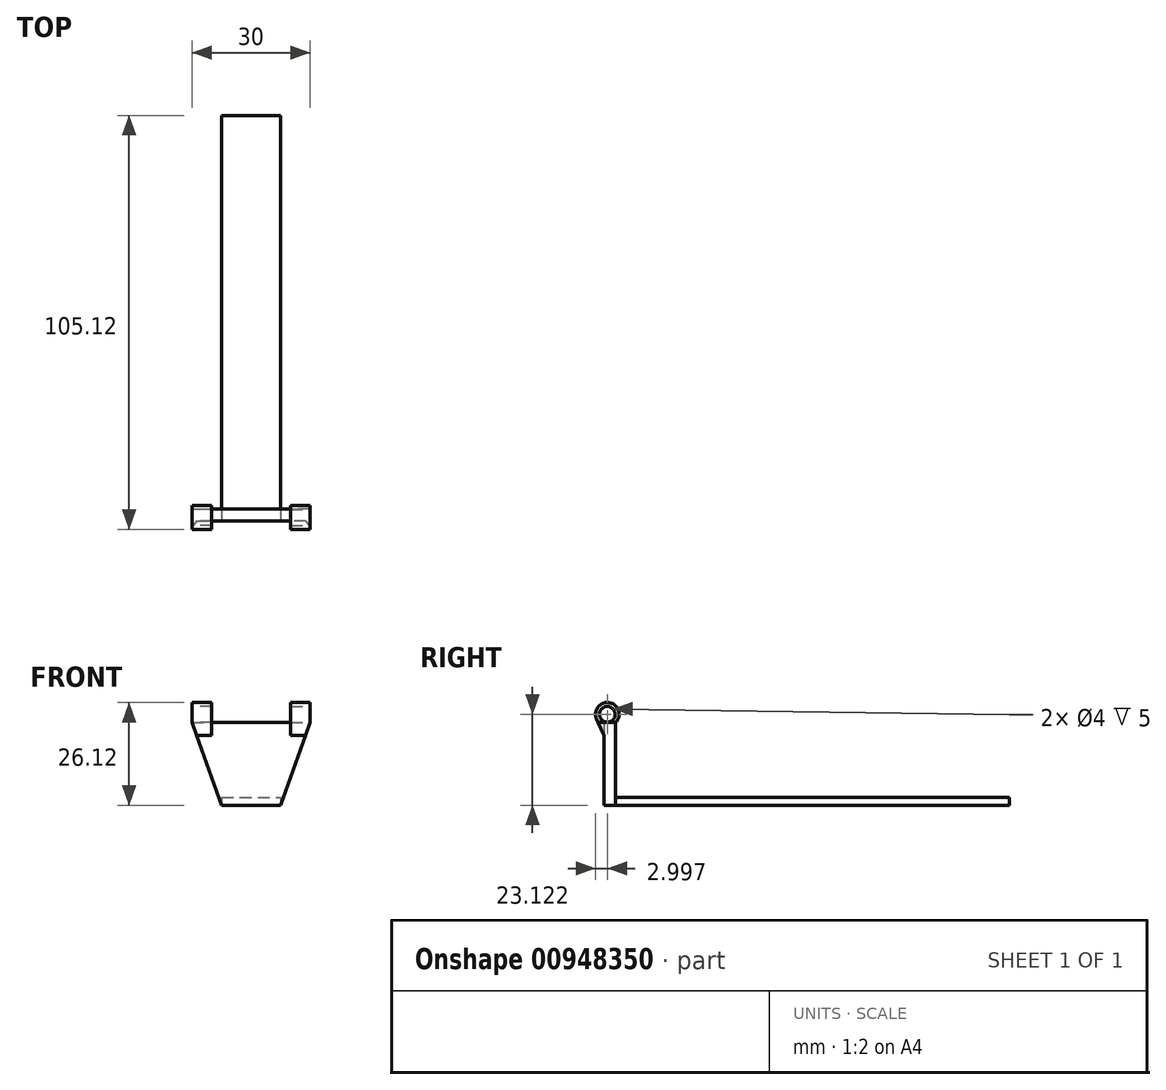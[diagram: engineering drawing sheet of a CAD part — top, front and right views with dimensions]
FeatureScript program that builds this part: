
annotation { "Feature Type Name" : "Feature", "Feature Type Description" : "" }
export const myFeature = defineFeature(function(context is Context, id is Id, definition is map)
    precondition{}
    {
        {
            var Q0;
            Q0=qCreatedBy(makeId("Top.planeOp"),FACE);
            var sketch = newSketch(context, id + "F0", { "sketchPlane" : qUnion([Q0])});
            skLineSegment(sketch, "E0.bottom", {"start": v(7.5, 51.5) * mm, "end": v(-7.5, 51.5) * mm});
            skLineSegment(sketch, "E0.top", {"start": v(7.5, -51.5) * mm, "end": v(-7.5, -51.5) * mm});
            skLineSegment(sketch, "E0.left", {"start": v(7.5, 51.5) * mm, "end": v(7.5, -51.5) * mm});
            skLineSegment(sketch, "E0.right", {"start": v(-7.5, 51.5) * mm, "end": v(-7.5, -51.5) * mm});
            skPoint(sketch, "E0.middle", {"position": v(0, 0) * mm});
            skSolve(sketch);
        }
        {
            var Q0;
            Q0=makeQuery(id+"F0.imprint","IMPRINT",FACE,{"disambiguationData":[TD([[makeQuery(id+"F0.imprint","IMPRINT",EDGE,{"derivedFrom":sQuery(id+"F0.wireOp",EDGE,"E0.bottom")}),1.0]])]});
            extrude(context, id + "F1", {"entities" : qUnion([Q0]), "depth" : 2 * mm, "offsetDistance" : 25 * mm});
        }
        {
            var Q0;
            Q0=makeQuery(id+"F1.opExtrude","CAP_FACE",FACE,{"disambiguationData":[OSD([sQuery(id+"F0.wireOp",EDGE,"E0.bottom"),sQuery(id+"F0.wireOp",EDGE,"E0.top"),sQuery(id+"F0.wireOp",EDGE,"E0.left"),sQuery(id+"F0.wireOp",EDGE,"E0.right")])],"isStart":false});
            var sketch = newSketch(context, id + "F2", { "sketchPlane" : qUnion([Q0])});
            skLineSegment(sketch, "E1.bottom", {"start": v(-7.5, -51.5) * mm, "end": v(7.5, -51.5) * mm});
            skLineSegment(sketch, "E1.top", {"start": v(-7.5, -48.5) * mm, "end": v(7.5, -48.5) * mm});
            skLineSegment(sketch, "E1.left", {"start": v(-7.5, -51.5) * mm, "end": v(-7.5, -48.5) * mm});
            skLineSegment(sketch, "E1.right", {"start": v(7.5, -51.5) * mm, "end": v(7.5, -48.5) * mm});
            skSolve(sketch);
        }
        {
            var Q0;
            Q0=makeQuery(id+"F2.imprint","IMPRINT",FACE,{"disambiguationData":[TD([[makeQuery(id+"F2.imprint","IMPRINT",EDGE,{"derivedFrom":sQuery(id+"F2.wireOp",EDGE,"E1.bottom")}),-1.0]])]});
            extrude(context, id + "F3", {"entities" : qUnion([Q0]), "operationType" : NewBodyOperationType.ADD, "depth" : 19 * mm, "offsetDistance" : 25 * mm});
        }
        {
            var Q0;
            Q0=makeQuery(id+"F3.boolean.opBoolean","MERGE",FACE,{"derivedFrom":[makeQuery(id+"F1.opExtrude","SWEPT_FACE",FACE,{"disambiguationData":[OSD([sQuery(id+"F0.wireOp",EDGE,"E0.top")])]}),makeQuery(id+"F3.opExtrude","SWEPT_FACE",FACE,{"disambiguationData":[OSD([sQuery(id+"F2.wireOp",EDGE,"E1.bottom")])]})]});
            var sketch = newSketch(context, id + "F4", { "sketchPlane" : qUnion([Q0])});
            skLineSegment(sketch, "E2", {"start": v(7.5, 21) * mm, "end": v(15, 21) * mm});
            skLineSegment(sketch, "E3", {"start": v(15, 21) * mm, "end": v(7.5, 0) * mm});
            skLineSegment(sketch, "E4", {"start": v(-7.5, 21) * mm, "end": v(-15, 21) * mm});
            skLineSegment(sketch, "E5", {"start": v(-15, 21) * mm, "end": v(-7.5, 0) * mm});
            skSolve(sketch);
        }
        {
            var Q0;
            Q0=makeQuery(id+"F4.imprint","IMPRINT",FACE,{"disambiguationData":[TD([[makeQuery(id+"F4.imprint","IMPRINT",EDGE,{"derivedFrom":sQuery(id+"F4.wireOp",EDGE,"E4")}),1.0]])]});
            var Q1;
            Q1=makeQuery(id+"F4.imprint","IMPRINT",FACE,{"disambiguationData":[TD([[makeQuery(id+"F4.imprint","IMPRINT",EDGE,{"derivedFrom":sQuery(id+"F4.wireOp",EDGE,"E2")}),-1.0]])]});
            extrude(context, id + "F5", {"entities" : qUnion([Q0, Q1]), "operationType" : NewBodyOperationType.ADD, "oppositeDirection" : true, "depth" : 3 * mm, "offsetDistance" : 25 * mm});
        }
        {
            var Q0;
            Q0=qCreatedBy(makeId("Right.planeOp"),FACE);
            cPlane(context, id + "F6", {"entities" : qUnion([Q0]), "cplaneType" : CPlaneType.OFFSET, "offset" : 15 * mm, "width" : 150 * mm, "height" : 150 * mm});
        }
        {
            var Q0;
            Q0=qCreatedBy(id+"F6.planeOp",FACE);
            var sketch = newSketch(context, id + "F7", { "sketchPlane" : qUnion([Q0])});
            skPoint(sketch, "E6", {"position": v(-48.5, 21) * mm});
            skLineSegment(sketch, "E7", {"start": v(-48.5, 21) * mm, "end": v(-51.22, 23.72) * mm});
            skCircle(sketch, "E8", {"center": v(-50.62, 23.12) * mm, "radius": 2 * mm});
            skCircle(sketch, "E9", {"center": v(-50.62, 23.12) * mm, "radius": 3 * mm});
            skLineSegment(sketch, "E10", {"start": v(-48.5, 11) * mm, "end": v(-53.36, 21.9) * mm});
            skLineSegment(sketch, "E11", {"start": v(-48.5, 21) * mm, "end": v(-48.5, 11) * mm});
            skSolve(sketch);
        }
        {
            var Q0;
            Q0=makeQuery(id+"F7.imprint","IMPRINT",FACE,{"disambiguationData":[TD([[makeQuery(id+"F7.imprint","IMPRINT",EDGE,{"derivedFrom":sQuery(id+"F7.wireOp",EDGE,"E8")}),-1.0]])]});
            var Q1;
            {var subQ2=sQuery(id+"F7.wireOp",EDGE,"E10");Q1=makeQuery(id+"F7.imprint","IMPRINT",FACE,{"disambiguationData":[TD([[makeQuery(id+"F7.imprint","IMPRINT",EDGE,{"derivedFrom":subQ2}),-1.0]])]});}
            extrude(context, id + "F8", {"entities" : qUnion([Q0, Q1]), "oppositeDirection" : true, "depth" : 5 * mm, "offsetDistance" : 25 * mm});
        }
        {
            var Q0;
            {var subQ0=sQuery(id+"F2.wireOp",EDGE,"E1.bottom");var subQ1=sQuery(id+"F0.wireOp",EDGE,"E0.top");Q0=makeQuery(id+"F5.boolean.opBoolean","MERGE",FACE,{"derivedFrom":[makeQuery(id+"F3.boolean.opBoolean","MERGE",FACE,{"derivedFrom":[makeQuery(id+"F1.opExtrude","SWEPT_FACE",FACE,{"disambiguationData":[OSD([subQ1])]}),makeQuery(id+"F3.opExtrude","SWEPT_FACE",FACE,{"disambiguationData":[OSD([subQ0])]})]}),makeQuery(id+"F5.opExtrude","CAP_FACE",FACE,{"disambiguationData":[OSD([subQ1,sQuery(id+"F0.wireOp",EDGE,"E0.left"),subQ0,sQuery(id+"F2.wireOp",EDGE,"E1.right"),sQuery(id+"F4.wireOp",EDGE,"E2"),sQuery(id+"F4.wireOp",EDGE,"E3")])],"isStart":true}),makeQuery(id+"F5.opExtrude","CAP_FACE",FACE,{"disambiguationData":[OSD([subQ1,sQuery(id+"F0.wireOp",EDGE,"E0.right"),subQ0,sQuery(id+"F2.wireOp",EDGE,"E1.left"),sQuery(id+"F4.wireOp",EDGE,"E4"),sQuery(id+"F4.wireOp",EDGE,"E5")])],"isStart":true})]});}
            var sketch = newSketch(context, id + "F9", { "sketchPlane" : qUnion([Q0])});
            skLineSegment(sketch, "E12", {"start": v(15, 21) * mm, "end": v(11.25, 10.5) * mm});
            skLineSegment(sketch, "E13", {"start": v(11.25, 10.5) * mm, "end": v(15, 10.5) * mm});
            skLineSegment(sketch, "E14", {"start": v(15, 10.5) * mm, "end": v(15, 21) * mm});
            skSolve(sketch);
        }
        {
            var Q0;
            Q0=makeQuery(id+"F9.imprint","IMPRINT",FACE,{"disambiguationData":[TD([[makeQuery(id+"F9.imprint","IMPRINT",EDGE,{"derivedFrom":sQuery(id+"F9.wireOp",EDGE,"E12")}),1.0]])]});
            extrude(context, id + "F10", {"entities" : qUnion([Q0]), "operationType" : NewBodyOperationType.REMOVE, "endBound" : BoundingType.SYMMETRIC, "oppositeDirection" : true, "depth" : 25 * mm, "offsetDistance" : 25 * mm});
        }
        {
            var Q0;
            Q0=makeQuery(id+"F8.opExtrude","SWEPT_BODY",BODY,{"disambiguationData":[OSD([sQuery(id+"F7.wireOp",EDGE,"E8"),sQuery(id+"F7.wireOp",EDGE,"E9"),sQuery(id+"F7.wireOp",EDGE,"E10"),sQuery(id+"F7.wireOp",EDGE,"E11")])]});
            var Q1;
            Q1=qCreatedBy(makeId("Right.planeOp"),FACE);
            mirror(context, id + "F11", {"operationType" : NewBodyOperationType.ADD, "entities" : qUnion([Q0]), "mirrorPlane" : qUnion([Q1])});
        }
    });
